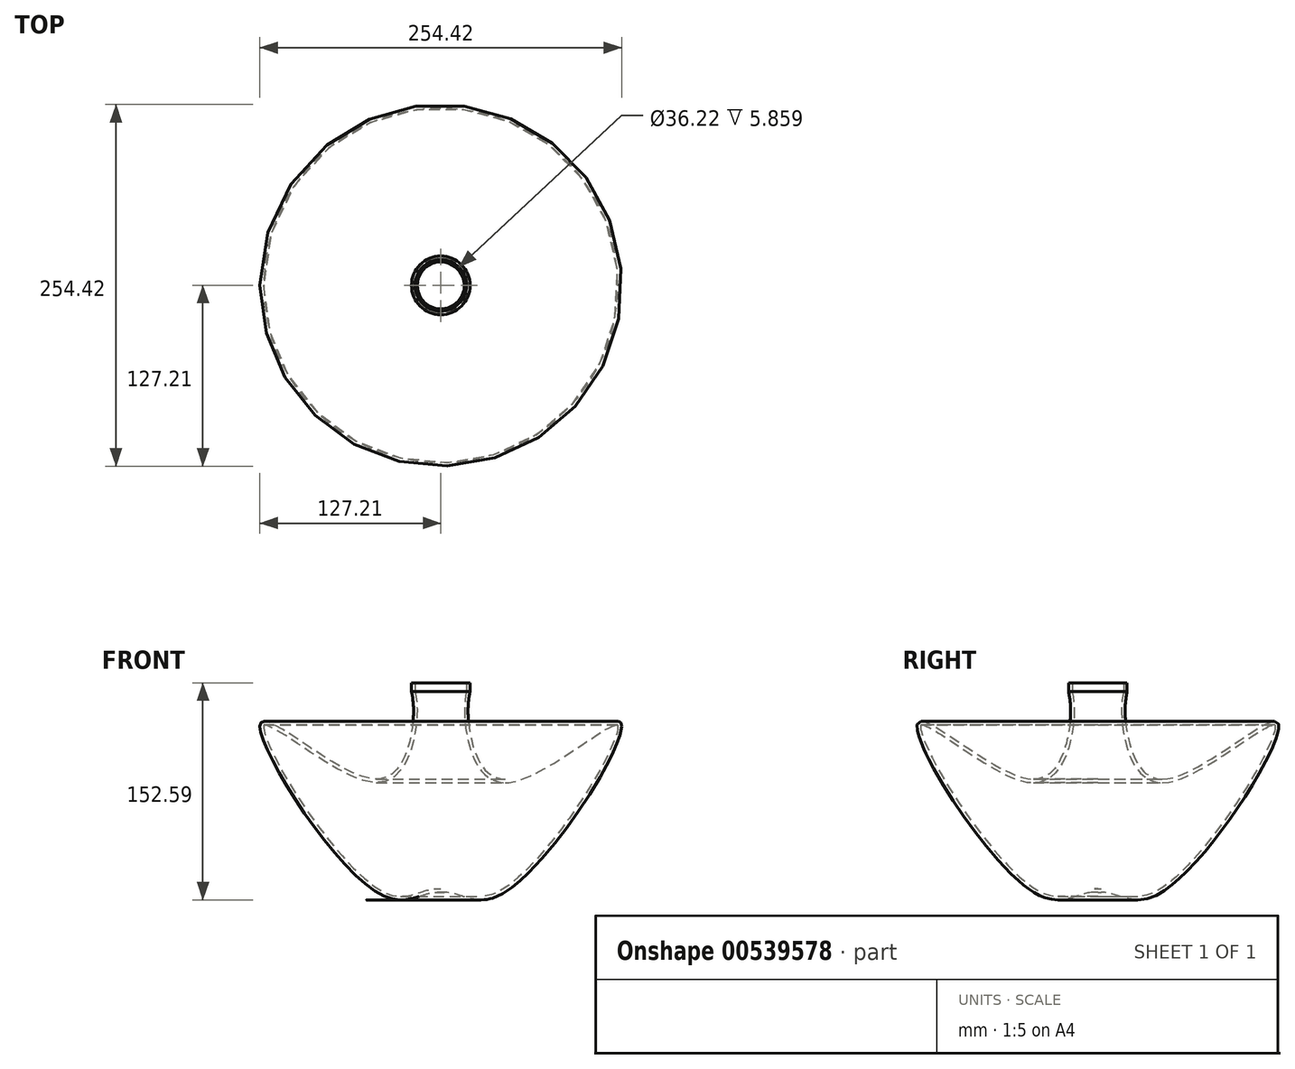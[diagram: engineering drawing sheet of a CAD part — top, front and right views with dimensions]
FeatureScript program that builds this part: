
annotation { "Feature Type Name" : "Feature", "Feature Type Description" : "" }
export const myFeature = defineFeature(function(context is Context, id is Id, definition is map)
    precondition{}
    {
        {
            var Q0;
            Q0=qCreatedBy(makeId("Front.planeOp"),FACE);
            var sketch = newSketch(context, id + "F0", { "sketchPlane" : qUnion([Q0])});
            skFitSpline(sketch, "E0", {"points": [v(-20.61, 81.37) * mm, v(-20.12, 55.63) * mm, v(-46.1, 19.84) * mm, v(-126.3, 59.88) * mm, v(-41.45, -61.8) * mm, v(0, -59.93) * mm], "startDerivative": vector(35.16, -159.62) * mm, "endDerivative": vector(222.5, -34.38) * mm});
            skLineSegment(sketch, "E1", {"start": v(0, -59.93) * mm, "end": v(0, 81.86) * mm});
            skLineSegment(sketch, "E2", {"start": v(-20.61, 81.37) * mm, "end": v(-20.61, 87.5) * mm});
            skLineSegment(sketch, "E3", {"start": v(0, 81.86) * mm, "end": v(0, 84.43) * mm});
            skPoint(sketch, "E3.endSnap0", {"position": v(-20.61, 84.43) * mm});
            skLineSegment(sketch, "E4", {"start": v(0, 84.43) * mm, "end": v(0, 87.5) * mm});
            skLineSegment(sketch, "E5", {"start": v(0, 87.5) * mm, "end": v(-20.61, 87.5) * mm});
            skSolve(sketch);
        }
        {
            var Q0;
            Q0=makeQuery(id+"F0.imprint","IMPRINT",FACE,{"disambiguationData":[TD([[makeQuery(id+"F0.imprint","IMPRINT",EDGE,{"derivedFrom":sQuery(id+"F0.wireOp",EDGE,"E0")}),1.0]])]});
            var Q1;
            Q1=sQuery(id+"F0.wireOp",EDGE,"E1");
            revolve(context, id + "F1", {"entities" : qUnion([Q0]), "axis" : qUnion([Q1]), "revolveType" : RevolveType.FULL});
        }
        {
            var Q0;
            Q0=makeQuery(id+"F1.opRevolve","SWEPT_FACE",FACE,{"disambiguationData":[OSD([sQuery(id+"F0.wireOp",EDGE,"E5")])]});
            shell(context, id + "F2", {"entities" : qUnion([Q0]), "thickness" : 2.5 * mm});
        }
    });
